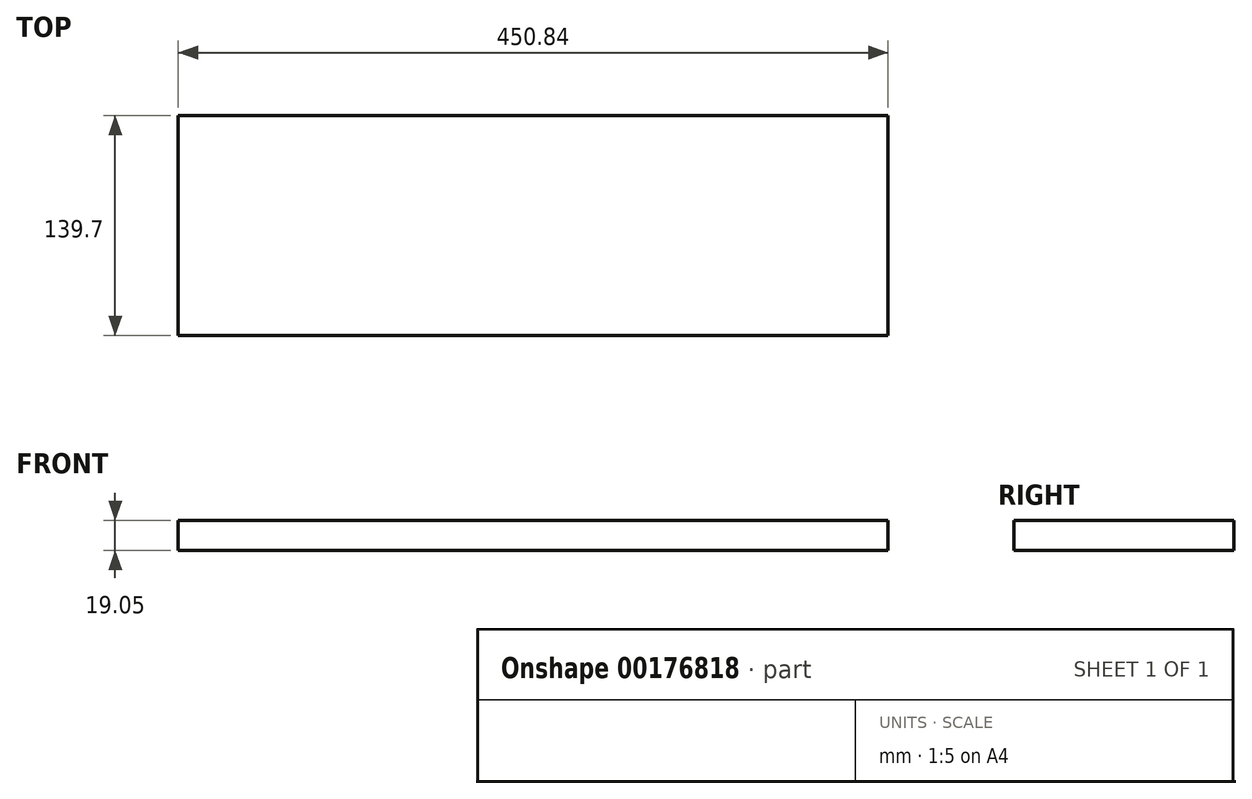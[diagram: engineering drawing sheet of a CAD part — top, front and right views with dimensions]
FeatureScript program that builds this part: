
annotation { "Feature Type Name" : "Feature", "Feature Type Description" : "" }
export const myFeature = defineFeature(function(context is Context, id is Id, definition is map)
    precondition{}
    {
        {
            var Q0;
            Q0=qCreatedBy(makeId("Top.planeOp"),FACE);
            var sketch = newSketch(context, id + "F0", { "sketchPlane" : qUnion([Q0])});
            skLineSegment(sketch, "E0.bottom", {"start": v(225.43, 69.85) * mm, "end": v(-225.43, 69.85) * mm});
            skLineSegment(sketch, "E0.top", {"start": v(225.43, -69.85) * mm, "end": v(-225.43, -69.85) * mm});
            skLineSegment(sketch, "E0.left", {"start": v(225.43, 69.85) * mm, "end": v(225.43, -69.85) * mm});
            skLineSegment(sketch, "E0.right", {"start": v(-225.43, 69.85) * mm, "end": v(-225.43, -69.85) * mm});
            skPoint(sketch, "E0.middle", {"position": v(0, 0) * mm});
            skSolve(sketch);
        }
        {
            var Q0;
            Q0 = qSketchRegion(id + "F0", true);
            extrude(context, id + "F1", {"entities" : qUnion([Q0]), "depth" : 19.05 * mm});
        }
    });
